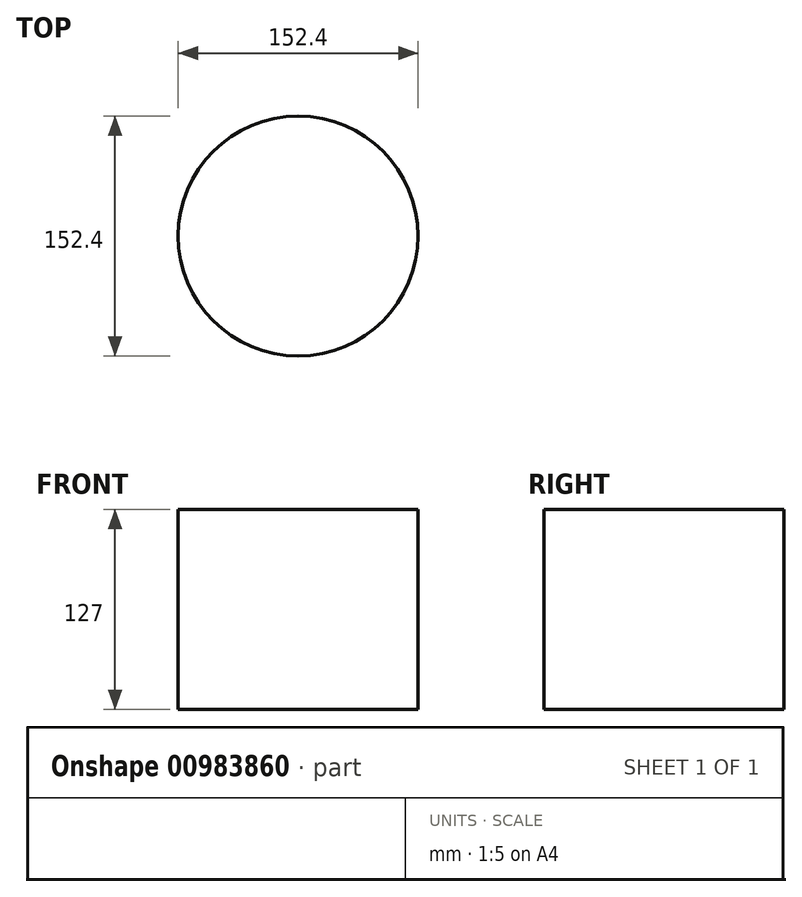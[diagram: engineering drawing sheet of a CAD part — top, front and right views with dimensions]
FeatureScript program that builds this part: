
annotation { "Feature Type Name" : "Feature", "Feature Type Description" : "" }
export const myFeature = defineFeature(function(context is Context, id is Id, definition is map)
    precondition{}
    {
        {
            var Q0;
            Q0=qCreatedBy(makeId("Top.planeOp"),FACE);
            var sketch = newSketch(context, id + "F0", { "sketchPlane" : qUnion([Q0])});
            skCircle(sketch, "E0", {"center": v(0, 0) * mm, "radius": 76.2 * mm});
            skSolve(sketch);
        }
        {
            var Q0;
            Q0=makeQuery(id+"F0.imprint","IMPRINT",FACE,{"disambiguationData":[TD([[makeQuery(id+"F0.imprint","IMPRINT",EDGE,{"derivedFrom":sQuery(id+"F0.wireOp",EDGE,"E0")}),1.0]])]});
            extrude(context, id + "F1", {"entities" : qUnion([Q0]), "depth" : 127 * mm, "offsetDistance" : 25.4 * mm});
        }
    });
